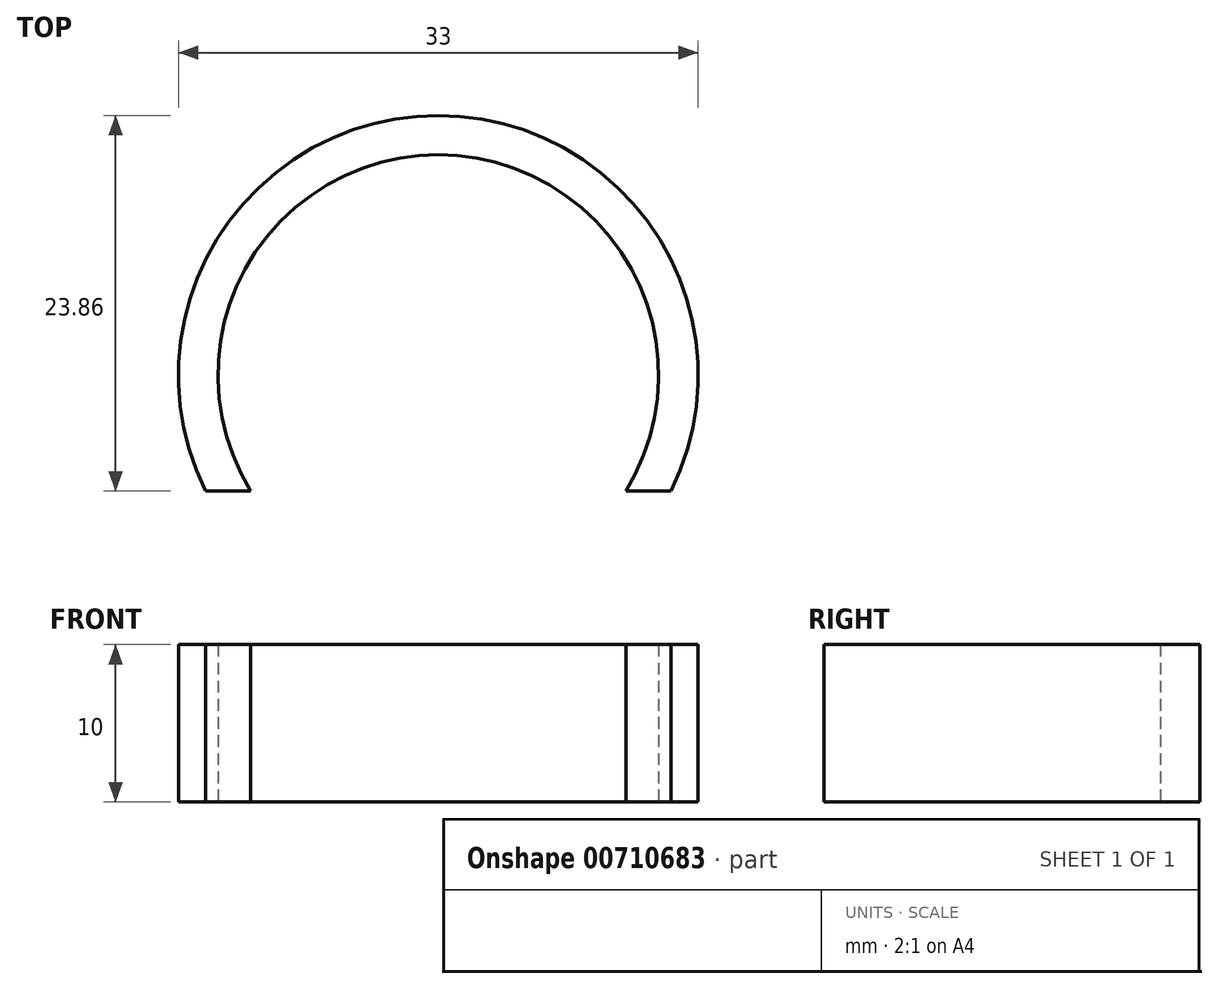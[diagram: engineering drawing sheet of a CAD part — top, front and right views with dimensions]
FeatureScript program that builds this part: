
annotation { "Feature Type Name" : "Feature", "Feature Type Description" : "" }
export const myFeature = defineFeature(function(context is Context, id is Id, definition is map)
    precondition{}
    {
        {
            var Q0;
            Q0=qCreatedBy(makeId("Top.planeOp"),FACE);
            var sketch = newSketch(context, id + "F0", { "sketchPlane" : qUnion([Q0])});
            skArc(sketch, "E0", {"start": v(13.42, -4) * mm, "mid": v(0, 14) * mm, "end": v(-13.42, -4) * mm});
            skArc(sketch, "E1", {"start": v(16, -4) * mm, "mid": v(0, 16.5) * mm, "end": v(-16, -4) * mm});
            skArc(sketch, "E2", {"start": v(-16, -4) * mm, "mid": v(-15.48, -5.71) * mm, "end": v(-14.77, -7.36) * mm});
            skArc(sketch, "E3", {"start": v(-13.42, -4) * mm, "mid": v(-12.77, -5.73) * mm, "end": v(-11.91, -7.36) * mm});
            skLineSegment(sketch, "E4", {"start": v(-14.77, -7.36) * mm, "end": v(-11.91, -7.36) * mm});
            skLineSegment(sketch, "E5.trimOffspring", {"start": v(11.91, -7.36) * mm, "end": v(14.77, -7.36) * mm});
            skArc(sketch, "E6.trimOffspring", {"start": v(14.77, -7.36) * mm, "mid": v(15.48, -5.71) * mm, "end": v(16, -4) * mm});
            skArc(sketch, "E7.trimOffspring", {"start": v(11.91, -7.36) * mm, "mid": v(12.77, -5.73) * mm, "end": v(13.42, -4) * mm});
            skSolve(sketch);
        }
        {
            var Q0;
            Q0=qSketchRegion(id+"F0",true);
            extrude(context, id + "F1", {"entities" : qUnion([Q0]), "depth" : 10 * mm, "offsetDistance" : 25 * mm});
        }
    });
